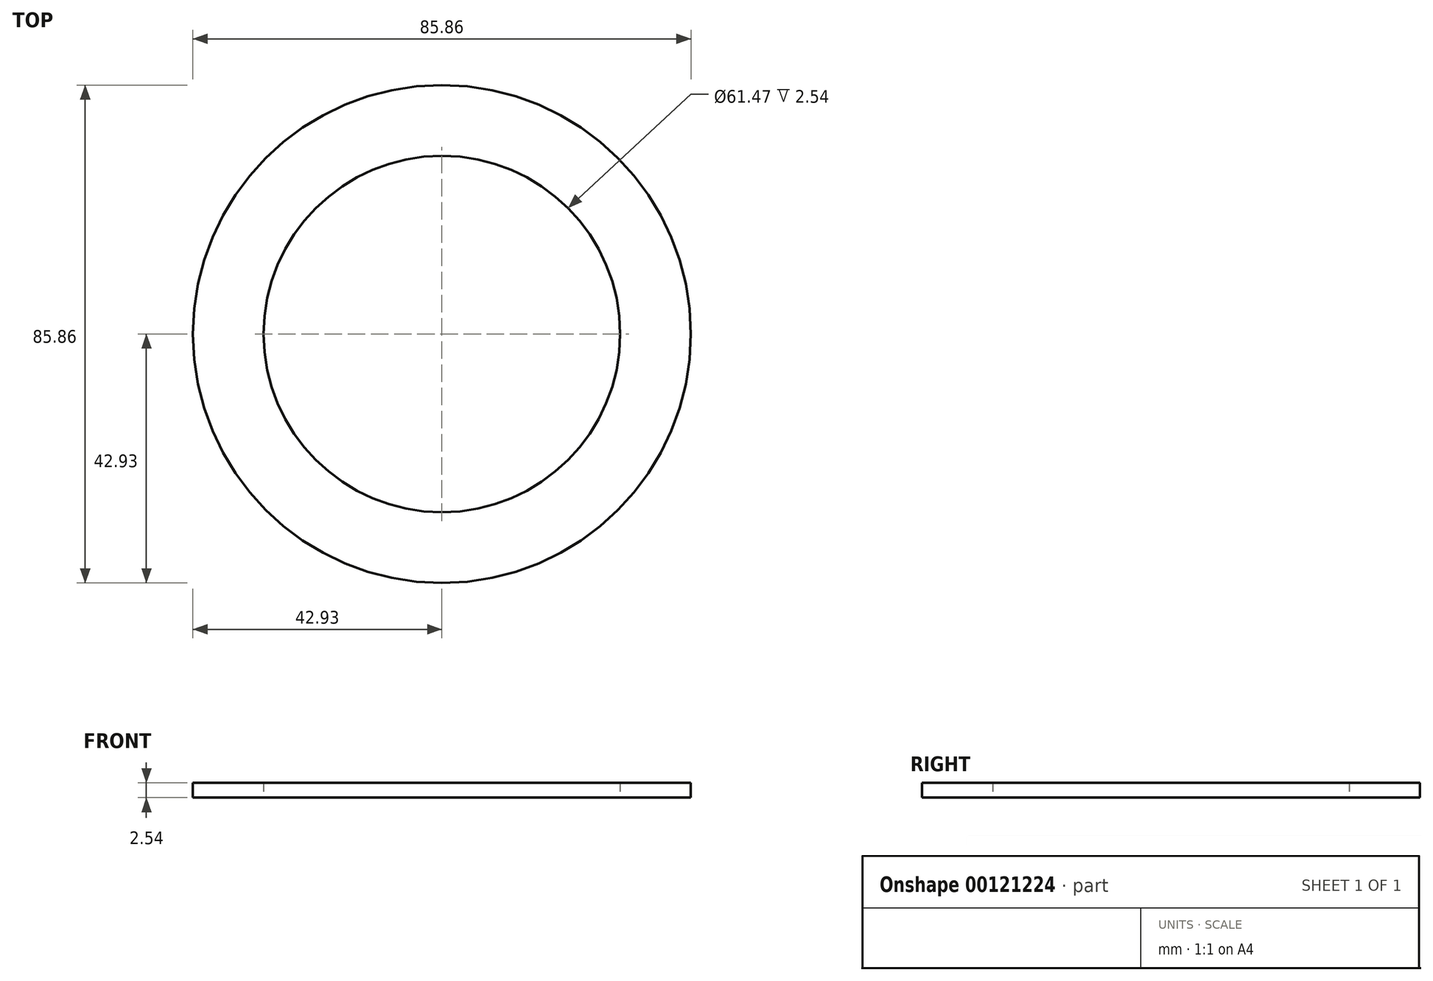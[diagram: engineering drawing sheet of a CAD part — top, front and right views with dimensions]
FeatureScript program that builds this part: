
annotation { "Feature Type Name" : "Feature", "Feature Type Description" : "" }
export const myFeature = defineFeature(function(context is Context, id is Id, definition is map)
    precondition{}
    {
        {
            var Q0;
            Q0=qCreatedBy(makeId("Top.planeOp"),FACE);
            var sketch = newSketch(context, id + "F0", { "sketchPlane" : qUnion([Q0])});
            skCircle(sketch, "E0", {"center": v(0, 0) * mm, "radius": 42.93 * mm});
            skCircle(sketch, "E1", {"center": v(0, 0) * mm, "radius": 30.73 * mm});
            skSolve(sketch);
        }
        {
            var Q0;
            Q0=makeQuery(id+"F0.imprint","IMPRINT",FACE,{"disambiguationData":[TD([[makeQuery(id+"F0.imprint","IMPRINT",EDGE,{"derivedFrom":sQuery(id+"F0.wireOp",EDGE,"E0")}),1.0]])]});
            extrude(context, id + "F1", {"entities" : qUnion([Q0]), "depth" : 2.54 * mm});
        }
    });
